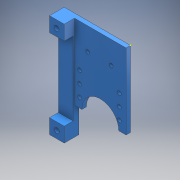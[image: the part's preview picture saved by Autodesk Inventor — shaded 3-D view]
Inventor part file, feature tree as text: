
AUTODESK INVENTOR PART (.ipt)
format: ipt  version: 2017 (Build 210142000, 142)  size: 198,144 bytes
history: native  units: mm
features: sketch x10, extrude x4, hole x3
ambient origin geometry x8: Origin, YZ Plane, XZ Plane, XY Plane, X Axis, Y Axis, Z Axis, Center Point
bodies: Solide1 (feature_tree)
feature tree (17):
  extrude  "Extrusion1"  Depth=25.0mm
  extrude  "Extrusion3"  Depth=35.0mm
  sketch  "Esquisse4"
  extrude  "Extrusion6"  Depth=10.0mm
  hole  "Perçage1"  [1 undecoded]
  sketch  "Esquisse9"
  sketch  "Esquisse10"
  hole  "Perçage2"  [1 undecoded]
  extrude  "Extrusion8"  Depth=35.0mm
  sketch  "Esquisse17"
  hole  "Perçage5"  [1 undecoded]
  sketch  "Esquisse1"
  sketch  "Esquisse3"
  sketch  "Esquisse7"
  sketch  "Esquisse8"
  sketch  "Esquisse11"
  sketch  "Esquisse18"
note: 3 required parameter values undecoded (feature->parameter linkage not recoverable at this tier; creation-order binding heuristic only, values carry confidence <= 0.55)
